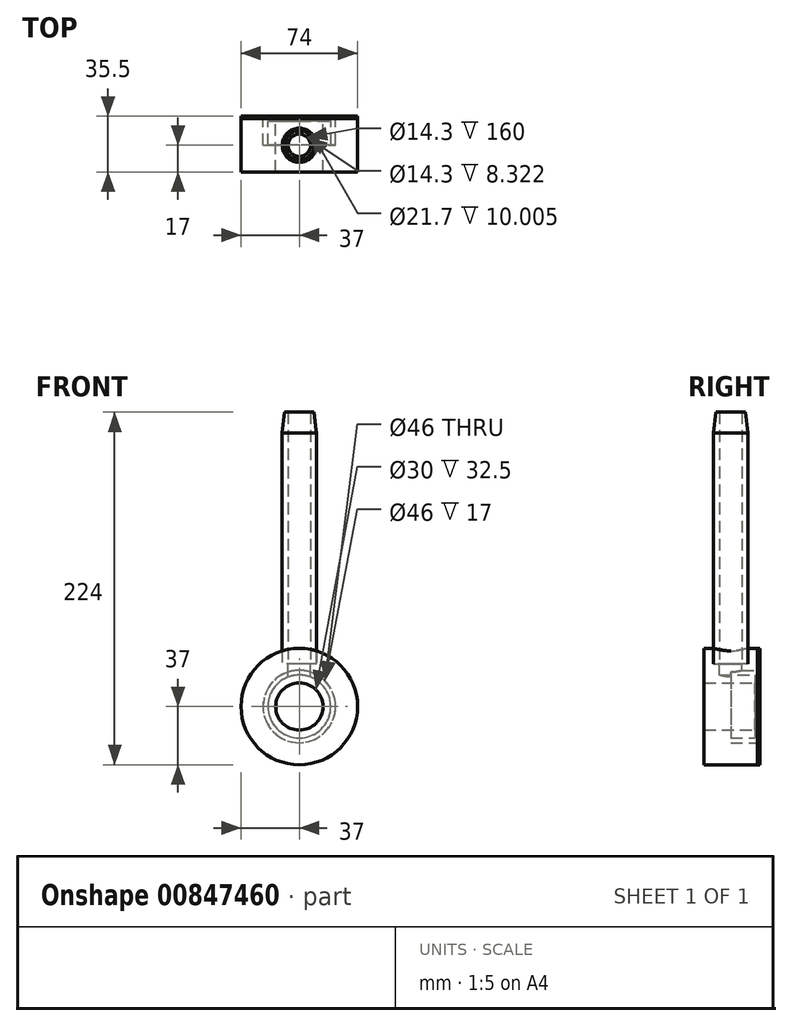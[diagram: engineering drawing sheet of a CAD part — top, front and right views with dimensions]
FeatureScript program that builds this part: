
annotation { "Feature Type Name" : "Feature", "Feature Type Description" : "" }
export const myFeature = defineFeature(function(context is Context, id is Id, definition is map)
    precondition{}
    {
        {
            var Q0;
            Q0=qCreatedBy(makeId("Front.planeOp"),FACE);
            var sketch = newSketch(context, id + "F0", { "sketchPlane" : qUnion([Q0])});
            skLineSegment(sketch, "E0", {"start": v(0, 117.35) * mm, "end": v(0, -120.95) * mm, "construction": true});
            skLineSegment(sketch, "E1", {"start": v(-113.16, 0) * mm, "end": v(131.1, 0) * mm, "construction": true});
            skCircle(sketch, "E2", {"center": v(0, 0) * mm, "radius": 37 * mm});
            skCircle(sketch, "E3", {"center": v(0, 0) * mm, "radius": 15 * mm});
            skSolve(sketch);
        }
        {
            var Q0;
            Q0 = qSketchRegion(id + "F0", true);
            extrude(context, id + "F1", {"entities" : qUnion([Q0]), "depth" : 34 * mm, "offsetDistance" : 25 * mm});
        }
        {
            var Q0;
            Q0=makeQuery(id+"F1.opExtrude","CAP_FACE",FACE,{"disambiguationData":[OSD([sQuery(id+"F0.wireOp",EDGE,"E2"),sQuery(id+"F0.wireOp",EDGE,"E3")])],"isStart":true});
            var sketch = newSketch(context, id + "F2", { "sketchPlane" : qUnion([Q0])});
            skCircle(sketch, "E4", {"center": v(0, 0) * mm, "radius": 23 * mm});
            skCircle(sketch, "E5.0", {"center": v(0, 0) * mm, "radius": 15 * mm});
            skSolve(sketch);
        }
        {
            var Q0;
            Q0 = qSketchRegion(id + "F2", true);
            extrude(context, id + "F3", {"entities" : qUnion([Q0]), "operationType" : NewBodyOperationType.REMOVE, "oppositeDirection" : true, "depth" : 1.5 * mm, "offsetDistance" : 25 * mm});
        }
        {
            var Q0;
            Q0=makeQuery(id+"F1.opExtrude","CAP_FACE",FACE,{"disambiguationData":[OSD([sQuery(id+"F0.wireOp",EDGE,"E2"),sQuery(id+"F0.wireOp",EDGE,"E3")])],"isStart":true});
            var sketch = newSketch(context, id + "F4", { "sketchPlane" : qUnion([Q0])});
            skCircle(sketch, "E6.0", {"center": v(0, 0) * mm, "radius": 23 * mm});
            skCircle(sketch, "E7.0", {"center": v(0, 0) * mm, "radius": 20 * mm});
            skSolve(sketch);
        }
        {
            var Q0;
            Q0 = qSketchRegion(id + "F4", true);
            extrude(context, id + "F5", {"entities" : qUnion([Q0]), "operationType" : NewBodyOperationType.REMOVE, "oppositeDirection" : true, "depth" : 17 * mm, "offsetDistance" : 25 * mm});
        }
        {
            var Q0;
            Q0=qCreatedBy(makeId("Top.planeOp"),FACE);
            cPlane(context, id + "F6", {"entities" : qUnion([Q0]), "cplaneType" : CPlaneType.OFFSET, "offset" : 37 * mm, "width" : 150 * mm, "height" : 150 * mm});
        }
        {
            var Q0;
            Q0=qCreatedBy(id+"F6.planeOp",FACE);
            var sketch = newSketch(context, id + "F7", { "sketchPlane" : qUnion([Q0])});
            skLineSegment(sketch, "E8", {"start": v(-60.75, 0) * mm, "end": v(57.59, 0) * mm, "construction": true});
            skLineSegment(sketch, "E9", {"start": v(-71.56, -17) * mm, "end": v(74.4, -17) * mm, "construction": true});
            skLineSegment(sketch, "E10", {"start": v(0, 44.87) * mm, "end": v(0, -60.25) * mm, "construction": true});
            skCircle(sketch, "E11", {"center": v(0, -17) * mm, "radius": 7.15 * mm});
            skSolve(sketch);
        }
        {
            var Q0;
            Q0 = qSketchRegion(id + "F7", true);
            var Q1;
            Q1=makeQuery(id+"F5.boolean.opBoolean","COPY",FACE,{"derivedFrom":makeQuery(id+"F5.opExtrude","SWEPT_FACE",FACE,{"disambiguationData":[OSD([sQuery(id+"F4.wireOp",EDGE,"E7.0")])]})});
            extrude(context, id + "F8", {"entities" : qUnion([Q0]), "operationType" : NewBodyOperationType.REMOVE, "endBound" : BoundingType.UP_TO_SURFACE, "oppositeDirection" : true, "depth" : 25 * mm, "endBoundEntityFace" : qUnion([Q1]), "offsetDistance" : 25 * mm});
        }
        {
            var Q0;
            Q0=qCreatedBy(id+"F6.planeOp",FACE);
            var sketch = newSketch(context, id + "F9", { "sketchPlane" : qUnion([Q0])});
            skLineSegment(sketch, "E12", {"start": v(0, 9.84) * mm, "end": v(0, -42.79) * mm, "construction": true});
            skLineSegment(sketch, "E13", {"start": v(-43.62, -17) * mm, "end": v(46.63, -17) * mm, "construction": true});
            skLineSegment(sketch, "E14", {"start": v(-46.77, 0) * mm, "end": v(54.26, 0) * mm, "construction": true});
            skCircle(sketch, "E15", {"center": v(0, -17) * mm, "radius": 10.85 * mm});
            skSolve(sketch);
        }
        {
            var Q0;
            Q0 = qSketchRegion(id + "F9", true);
            extrude(context, id + "F10", {"entities" : qUnion([Q0]), "operationType" : NewBodyOperationType.REMOVE, "oppositeDirection" : true, "depth" : 10 * mm, "offsetDistance" : 25 * mm});
        }
        {
            var Q0;
            Q0=makeQuery(id+"F10.boolean.opBoolean","COPY",FACE,{"derivedFrom":makeQuery(id+"F10.opExtrude","CAP_FACE",FACE,{"disambiguationData":[OSD([sQuery(id+"F9.wireOp",EDGE,"E15")])],"isStart":false})});
            var sketch = newSketch(context, id + "F11", { "sketchPlane" : qUnion([Q0])});
            skCircle(sketch, "E16.0", {"center": v(0, -17) * mm, "radius": 10.85 * mm});
            skCircle(sketch, "E17.0", {"center": v(0, -17) * mm, "radius": 7.15 * mm});
            skSolve(sketch);
        }
        {
            var Q0;
            Q0 = qSketchRegion(id + "F11", true);
            extrude(context, id + "F12", {"entities" : qUnion([Q0]), "depth" : 160 * mm, "offsetDistance" : 25 * mm});
        }
        {
            var Q0;
            Q0=makeQuery(id+"F12.opExtrude","CAP_EDGE",EDGE,{"disambiguationData":[OSD([sQuery(id+"F11.wireOp",EDGE,"E16.0")])],"isStart":false});
            chamfer(context, id + "F13", {"entities" : qUnion([Q0]), "chamferType" : ChamferType.TWO_OFFSETS, "width1" : 1.53 * mm, "oppositeDirection" : false, "width2" : 13.16 * mm, "tangentPropagation" : true});
        }
        {
            var Q0;
            Q0=makeQuery(id+"F1.opExtrude","CAP_FACE",FACE,{"disambiguationData":[OSD([sQuery(id+"F0.wireOp",EDGE,"E2"),sQuery(id+"F0.wireOp",EDGE,"E3")])],"isStart":true});
            var sketch = newSketch(context, id + "F14", { "sketchPlane" : qUnion([Q0])});
            skCircle(sketch, "E18.0", {"center": v(0, 0) * mm, "radius": 37 * mm});
            skCircle(sketch, "E19.0", {"center": v(0, 0) * mm, "radius": 23 * mm});
            skSolve(sketch);
        }
        {
            var Q0;
            Q0 = qSketchRegion(id + "F14", true);
            extrude(context, id + "F15", {"entities" : qUnion([Q0]), "depth" : 1.5 * mm, "offsetDistance" : 25 * mm});
        }
    });
